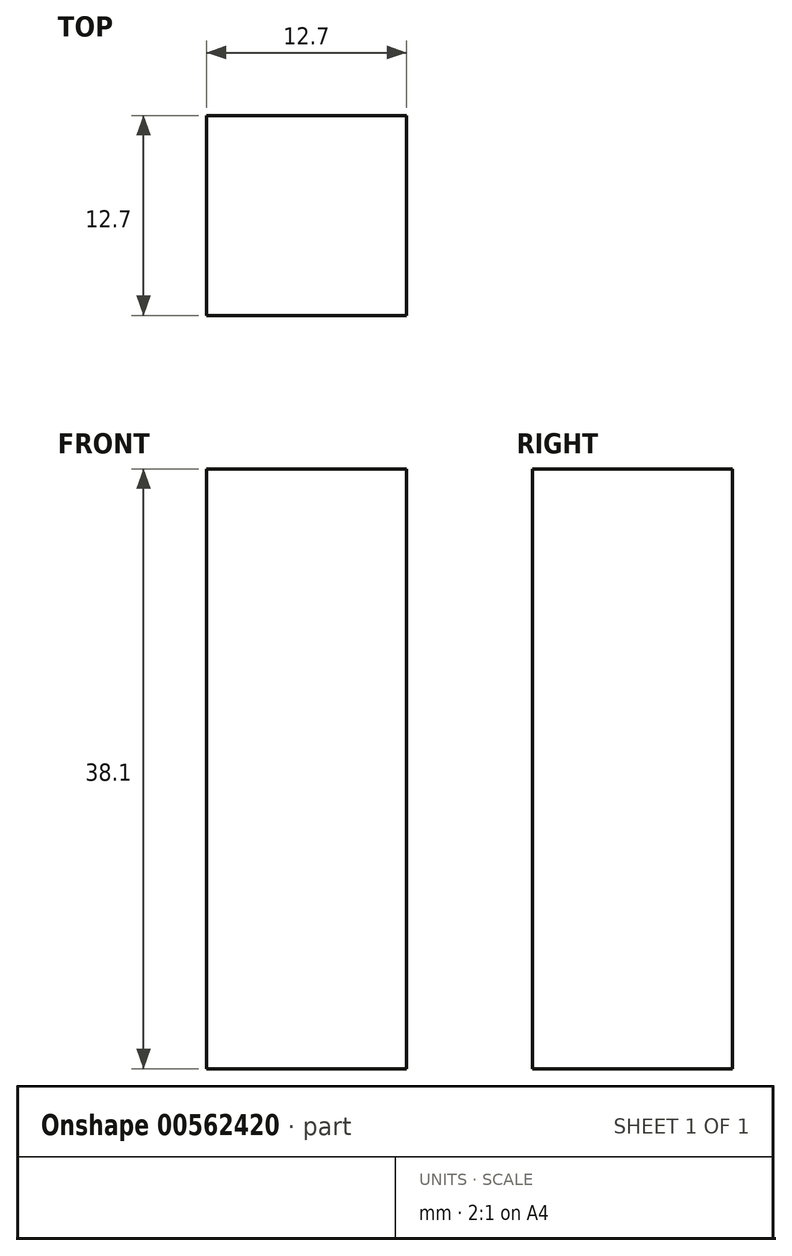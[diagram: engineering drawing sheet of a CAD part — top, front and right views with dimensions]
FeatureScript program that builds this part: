
annotation { "Feature Type Name" : "Feature", "Feature Type Description" : "" }
export const myFeature = defineFeature(function(context is Context, id is Id, definition is map)
    precondition{}
    {
        {
            var Q0;
            Q0=qCreatedBy(makeId("Top.planeOp"),FACE);
            var sketch = newSketch(context, id + "F0", { "sketchPlane" : qUnion([Q0])});
            skLineSegment(sketch, "E0.bottom", {"start": v(-10.46, 23.21) * mm, "end": v(2.24, 23.21) * mm});
            skLineSegment(sketch, "E0.top", {"start": v(-10.46, 10.51) * mm, "end": v(2.24, 10.51) * mm});
            skLineSegment(sketch, "E0.left", {"start": v(-10.46, 23.21) * mm, "end": v(-10.46, 10.51) * mm});
            skLineSegment(sketch, "E0.right", {"start": v(2.24, 23.21) * mm, "end": v(2.24, 10.51) * mm});
            skSolve(sketch);
        }
        {
            var Q0;
            Q0 = qSketchRegion(id + "F0", true);
            extrude(context, id + "F1", {"entities" : qUnion([Q0]), "depth" : 38.1 * mm, "offsetDistance" : 25.4 * mm});
        }
    });
